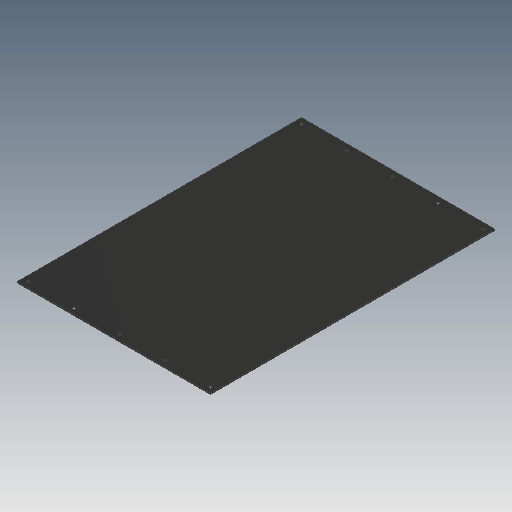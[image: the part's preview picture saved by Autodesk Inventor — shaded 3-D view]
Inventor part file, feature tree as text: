
AUTODESK INVENTOR PART (.ipt)
format: ipt  version: 2018.2 (Build 222227000, 227)  size: 101,888 bytes
history: native  units: mm
features: sketch x2, extrude x1, hole x1, pattern_linear x1, projected_geometry x1
ambient origin geometry x8: Origin, YZ Plane, XZ Plane, XY Plane, X Axis, Y Axis, Z Axis, Center Point
bodies: Solid1 (feature_tree)
feature tree (6):
  extrude  "Extrusion1"  Depth=500.0mm
  hole  "Hole1"  [1 undecoded]
  pattern_linear  "Rectangular Pattern1"  Spacing1=10.0mm  [1 undecoded]
  sketch  "Sketch1"  dims[d0=340.0mm d1=500.0mm]
  sketch  "Sketch2"  dims[d2=1.5875mm d3=0.0mm d4=10.0mm d5=10.0mm d6=5.5mm d7=6.0mm d8=12.24mm d9=3.58mm d10=90.0deg d11=8.0mm d12=20.594885mm d13=20.0mm d15=480.0mm d16=50.0mm d18=80.0mm]
  projected_geometry  "Projected Loop1"
note: 2 required parameter values undecoded (feature->parameter linkage not recoverable at this tier; creation-order binding heuristic only, values carry confidence <= 0.55)
